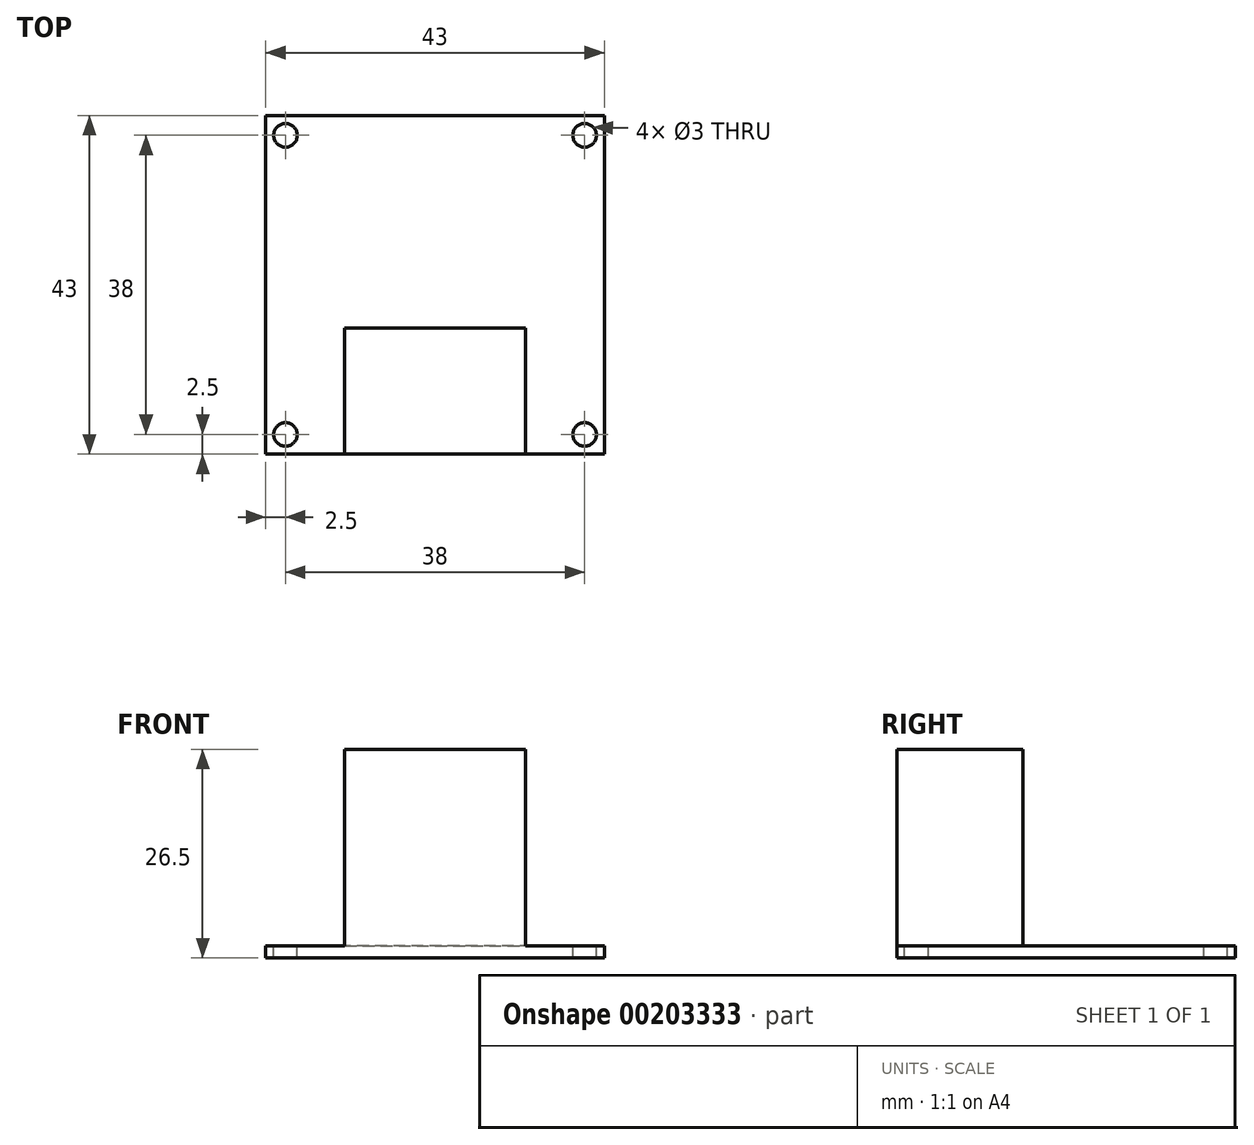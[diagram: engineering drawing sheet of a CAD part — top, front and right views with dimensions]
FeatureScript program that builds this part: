
annotation { "Feature Type Name" : "Feature", "Feature Type Description" : "" }
export const myFeature = defineFeature(function(context is Context, id is Id, definition is map)
    precondition{}
    {
        {
            var Q0;
            Q0=qCreatedBy(makeId("Top.planeOp"),FACE);
            var sketch = newSketch(context, id + "F0", { "sketchPlane" : qUnion([Q0])});
            skLineSegment(sketch, "E0.bottom", {"start": v(21.5, -21.5) * mm, "end": v(-21.5, -21.5) * mm});
            skLineSegment(sketch, "E0.top", {"start": v(21.5, 21.5) * mm, "end": v(-21.5, 21.5) * mm});
            skLineSegment(sketch, "E0.left", {"start": v(21.5, -21.5) * mm, "end": v(21.5, 21.5) * mm});
            skLineSegment(sketch, "E0.right", {"start": v(-21.5, -21.5) * mm, "end": v(-21.5, 21.5) * mm});
            skPoint(sketch, "E0.middle", {"position": v(0, 0) * mm});
            skSolve(sketch);
        }
        {
            var Q0;
            Q0 = qSketchRegion(id + "F0", true);
            extrude(context, id + "F1", {"entities" : qUnion([Q0]), "depth" : 1.5 * mm});
        }
        {
            var Q0;
            Q0=makeQuery(id+"F1.opExtrude","CAP_FACE",FACE,{"disambiguationData":[OSD([sQuery(id+"F0.wireOp",EDGE,"E0.bottom"),sQuery(id+"F0.wireOp",EDGE,"E0.top"),sQuery(id+"F0.wireOp",EDGE,"E0.left"),sQuery(id+"F0.wireOp",EDGE,"E0.right")])],"isStart":false});
            var sketch = newSketch(context, id + "F2", { "sketchPlane" : qUnion([Q0])});
            skLineSegment(sketch, "E1.bottom", {"start": v(-11.5, -21.5) * mm, "end": v(11.5, -21.5) * mm});
            skLineSegment(sketch, "E1.top", {"start": v(-11.5, -5.5) * mm, "end": v(11.5, -5.5) * mm});
            skLineSegment(sketch, "E1.left", {"start": v(-11.5, -21.5) * mm, "end": v(-11.5, -5.5) * mm});
            skLineSegment(sketch, "E1.right", {"start": v(11.5, -21.5) * mm, "end": v(11.5, -5.5) * mm});
            skSolve(sketch);
        }
        {
            var Q0;
            Q0 = qSketchRegion(id + "F2", true);
            extrude(context, id + "F3", {"entities" : qUnion([Q0]), "operationType" : NewBodyOperationType.ADD, "depth" : 25 * mm});
        }
        {
            var Q0;
            Q0=makeQuery(id+"F1.opExtrude","CAP_FACE",FACE,{"disambiguationData":[OSD([sQuery(id+"F0.wireOp",EDGE,"E0.bottom"),sQuery(id+"F0.wireOp",EDGE,"E0.top"),sQuery(id+"F0.wireOp",EDGE,"E0.left"),sQuery(id+"F0.wireOp",EDGE,"E0.right")])],"isStart":false});
            var sketch = newSketch(context, id + "F4", { "sketchPlane" : qUnion([Q0])});
            skLineSegment(sketch, "E2", {"start": v(-21.5, 0) * mm, "end": v(21.5, 0) * mm, "construction": true});
            skLineSegment(sketch, "E3", {"start": v(0, 21.5) * mm, "end": v(0, -5.5) * mm, "construction": true});
            skCircle(sketch, "E4", {"center": v(-19, -19) * mm, "radius": 1.5 * mm});
            skCircle(sketch, "E5.MirrorC", {"center": v(19, -19) * mm, "radius": 1.5 * mm});
            skCircle(sketch, "E6.MirrorC", {"center": v(-19, 19) * mm, "radius": 1.5 * mm});
            skCircle(sketch, "E7.MirrorC", {"center": v(19, 19) * mm, "radius": 1.5 * mm});
            skSolve(sketch);
        }
        {
            var Q0;
            Q0 = qSketchRegion(id + "F4", true);
            extrude(context, id + "F5", {"entities" : qUnion([Q0]), "operationType" : NewBodyOperationType.REMOVE, "endBound" : BoundingType.THROUGH_ALL, "oppositeDirection" : true, "depth" : 25 * mm});
        }
    });
